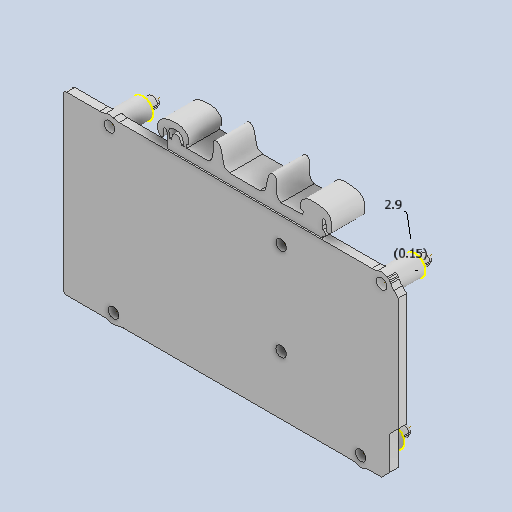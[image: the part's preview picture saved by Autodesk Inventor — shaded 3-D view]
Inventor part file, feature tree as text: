
AUTODESK INVENTOR PART (.ipt)
format: ipt  version: 2023 (Build 270158030, 158C)  size: 630,272 bytes
history: native  units: mm
features: other x19, reference x7, extrude x6, fillet x5, sketch x5, projected_geometry x2
ambient origin geometry x8: Origin, YZ Plane, XZ Plane, XY Plane, X Axis, Y Axis, Z Axis, Center Point
bodies: Body1 (feature_tree)
feature tree (44):
  other  "backplate"
  other  "Blocks"
  extrude  "Extrusion1"  Depth=1.5mm
  extrude  "Extrusion2"  Depth=10.0mm TaperAngle=0.0deg
  fillet  "Fillet2"  Radius=5.0mm
  extrude  "Extrusion3"  Depth=10.0mm TaperAngle=0.0deg
  fillet  "Fillet3"  Radius=7.0mm
  fillet  "Fillet4"  Radius=2.0mm
  fillet  "Fillet5"  Radius=5.0mm
  sketch  "Sketch4"  dims[d14=2.9mm d15=0.15mm]
  extrude  "Extrusion4"  Depth=0.15mm
  extrude  "Extrusion5"  Depth=1.0mm
  other  "Work Axis1"
  other  "Work Axis2"
  other  "Work Axis3"
  other  "Work Axis4"
  other  "Work Axis5"
  other  "Work Axis6"
  extrude  "Extrusion6"  Depth=1.0mm
  fillet  "Fillet6"  Radius=3.0mm
  sketch  "Sketch1"  dims[d0=6.2mm d1=1.5mm]
  reference  "Reference1"
  reference  "Reference2"
  reference  "Reference3"
  reference  "Reference4"
  reference  "Reference5"
  reference  "Reference6"
  sketch  "Sketch2"  dims[d2=10.0mm d3=0.0mm d4=2.5mm d5=0.0mm d7=5.0mm]
  reference  "Reference7"
  sketch  "Sketch3"  dims[d8=23.0mm d9=10.0mm d10=0.0mm d11=7.0mm d12=2.0mm d13=5.0mm]
  other  "din-rail-clip-outline"
  projected_geometry  "Projected Loop1"
  projected_geometry  "Projected Loop2"
  sketch  "Sketch6"  dims[d16=2.0mm d17=0.0mm d18=4.0mm d19=0.872665mm d21=0.4mm d25=3.0mm d26=0.0mm d27=1.0mm d30=1.759846mm d31=1.271846mm d32=3.0mm d28=0.5mm d29=0.872665mm]
  other  "crosscut"
  other  "arduino-DIN-mount.iam"
  other  "arduinoMegaDetailed:1"
  other  "din-rail-clip-outline:1"
  other  "crosscut:1"
  other  "crosscut:2"
  other  "crosscut:3"
  other  "crosscut:4"
  other  "crosscut:5"
  other  "crosscut:6"
